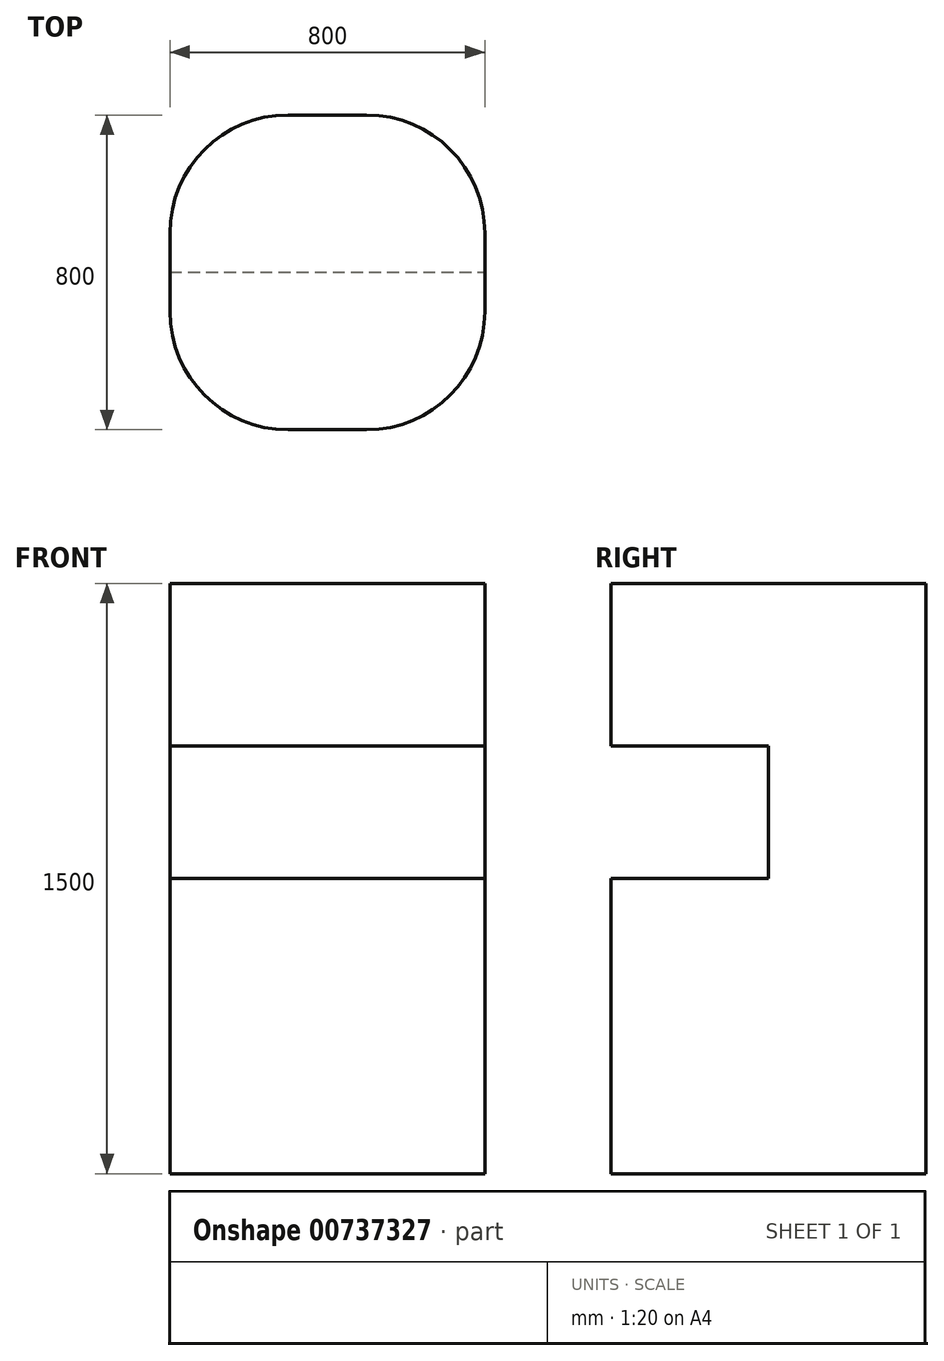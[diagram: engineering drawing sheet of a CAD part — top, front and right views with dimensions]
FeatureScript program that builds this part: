
annotation { "Feature Type Name" : "Feature", "Feature Type Description" : "" }
export const myFeature = defineFeature(function(context is Context, id is Id, definition is map)
    precondition{}
    {
        {
            var Q0;
            Q0=qCreatedBy(makeId("Top.planeOp"),FACE);
            var sketch = newSketch(context, id + "F0", { "sketchPlane" : qUnion([Q0])});
            skLineSegment(sketch, "E0.bottom", {"start": v(-404.41, 346.14) * mm, "end": v(395.59, 346.14) * mm});
            skLineSegment(sketch, "E0.top", {"start": v(-404.41, -453.86) * mm, "end": v(395.59, -453.86) * mm});
            skLineSegment(sketch, "E0.left", {"start": v(-404.41, 346.14) * mm, "end": v(-404.41, -453.86) * mm});
            skLineSegment(sketch, "E0.right", {"start": v(395.59, 346.14) * mm, "end": v(395.59, -453.86) * mm});
            skSolve(sketch);
        }
        {
            var Q0;
            Q0 = qSketchRegion(id + "F0", true);
            extrude(context, id + "F1", {"entities" : qUnion([Q0]), "depth" : 1500 * mm, "offsetDistance" : 25 * mm});
        }
        {
            var Q0;
            Q0=makeQuery(id+"F1.opExtrude","SWEPT_FACE",FACE,{"disambiguationData":[OSD([sQuery(id+"F0.wireOp",EDGE,"E0.top")])]});
            var sketch = newSketch(context, id + "F2", { "sketchPlane" : qUnion([Q0])});
            skLineSegment(sketch, "E1.bottom", {"start": v(-404.41, 1086.83) * mm, "end": v(395.59, 1086.83) * mm});
            skLineSegment(sketch, "E1.top", {"start": v(-404.41, 750) * mm, "end": v(395.59, 750) * mm});
            skLineSegment(sketch, "E1.left", {"start": v(-404.41, 1086.83) * mm, "end": v(-404.41, 750) * mm});
            skLineSegment(sketch, "E1.right", {"start": v(395.59, 1086.83) * mm, "end": v(395.59, 750) * mm});
            skSolve(sketch);
        }
        {
            var Q0;
            Q0 = qSketchRegion(id + "F2", true);
            extrude(context, id + "F3", {"entities" : qUnion([Q0]), "operationType" : NewBodyOperationType.REMOVE, "oppositeDirection" : true, "depth" : 400 * mm, "offsetDistance" : 25 * mm});
        }
        {
            var Q0;
            Q0=makeQuery(id+"F1.opExtrude","SWEPT_EDGE",EDGE,{"disambiguationData":[OSD([sQuery(id+"F0.wireOp",EDGE,"E0.bottom"),sQuery(id+"F0.wireOp",EDGE,"E0.left")])]});
            var Q1;
            Q1=makeQuery(id+"F1.opExtrude","SWEPT_EDGE",EDGE,{"disambiguationData":[OSD([sQuery(id+"F0.wireOp",EDGE,"E0.bottom"),sQuery(id+"F0.wireOp",EDGE,"E0.right")])]});
            var Q2;
            {var subQ0=sQuery(id+"F0.wireOp",EDGE,"E0.left");var subQ1=sQuery(id+"F0.wireOp",EDGE,"E0.top");Q2=makeQuery(id+"F3.boolean.opBoolean","SPLIT",EDGE,{"disambiguationData":[TD([makeQuery(id+"F3.opExtrude","SWEPT_FACE",FACE,{"disambiguationData":[OSD([sQuery(id+"F2.wireOp",EDGE,"E1.bottom")])]})])],"derivedFrom":makeQuery(id+"F1.opExtrude","SWEPT_EDGE",EDGE,{"disambiguationData":[OSD([subQ1,subQ0])]})});}
            var Q3;
            {var subQ0=sQuery(id+"F0.wireOp",EDGE,"E0.left");var subQ1=sQuery(id+"F0.wireOp",EDGE,"E0.top");Q3=makeQuery(id+"F3.boolean.opBoolean","SPLIT",EDGE,{"disambiguationData":[TD([makeQuery(id+"F3.opExtrude","SWEPT_FACE",FACE,{"disambiguationData":[OSD([sQuery(id+"F2.wireOp",EDGE,"E1.top")])]})])],"derivedFrom":makeQuery(id+"F1.opExtrude","SWEPT_EDGE",EDGE,{"disambiguationData":[OSD([subQ1,subQ0])]})});}
            var Q4;
            {var subQ0=sQuery(id+"F0.wireOp",EDGE,"E0.right");var subQ1=sQuery(id+"F0.wireOp",EDGE,"E0.top");Q4=makeQuery(id+"F3.boolean.opBoolean","SPLIT",EDGE,{"disambiguationData":[TD([makeQuery(id+"F3.opExtrude","SWEPT_FACE",FACE,{"disambiguationData":[OSD([sQuery(id+"F2.wireOp",EDGE,"E1.bottom")])]})])],"derivedFrom":makeQuery(id+"F1.opExtrude","SWEPT_EDGE",EDGE,{"disambiguationData":[OSD([subQ1,subQ0])]})});}
            var Q5;
            {var subQ0=sQuery(id+"F0.wireOp",EDGE,"E0.right");var subQ1=sQuery(id+"F0.wireOp",EDGE,"E0.top");Q5=makeQuery(id+"F3.boolean.opBoolean","SPLIT",EDGE,{"disambiguationData":[TD([makeQuery(id+"F3.opExtrude","SWEPT_FACE",FACE,{"disambiguationData":[OSD([sQuery(id+"F2.wireOp",EDGE,"E1.top")])]})])],"derivedFrom":makeQuery(id+"F1.opExtrude","SWEPT_EDGE",EDGE,{"disambiguationData":[OSD([subQ1,subQ0])]})});}
            fillet(context, id + "F4", {"entities" : qUnion([Q0, Q1, Q2, Q3, Q4, Q5]), "tangentPropagation" : true, "radius" : 300 * mm, "defaultsChanged" : false, "vertexSettings" : [], "allowEdgeOverflow" : false});
        }
    });
